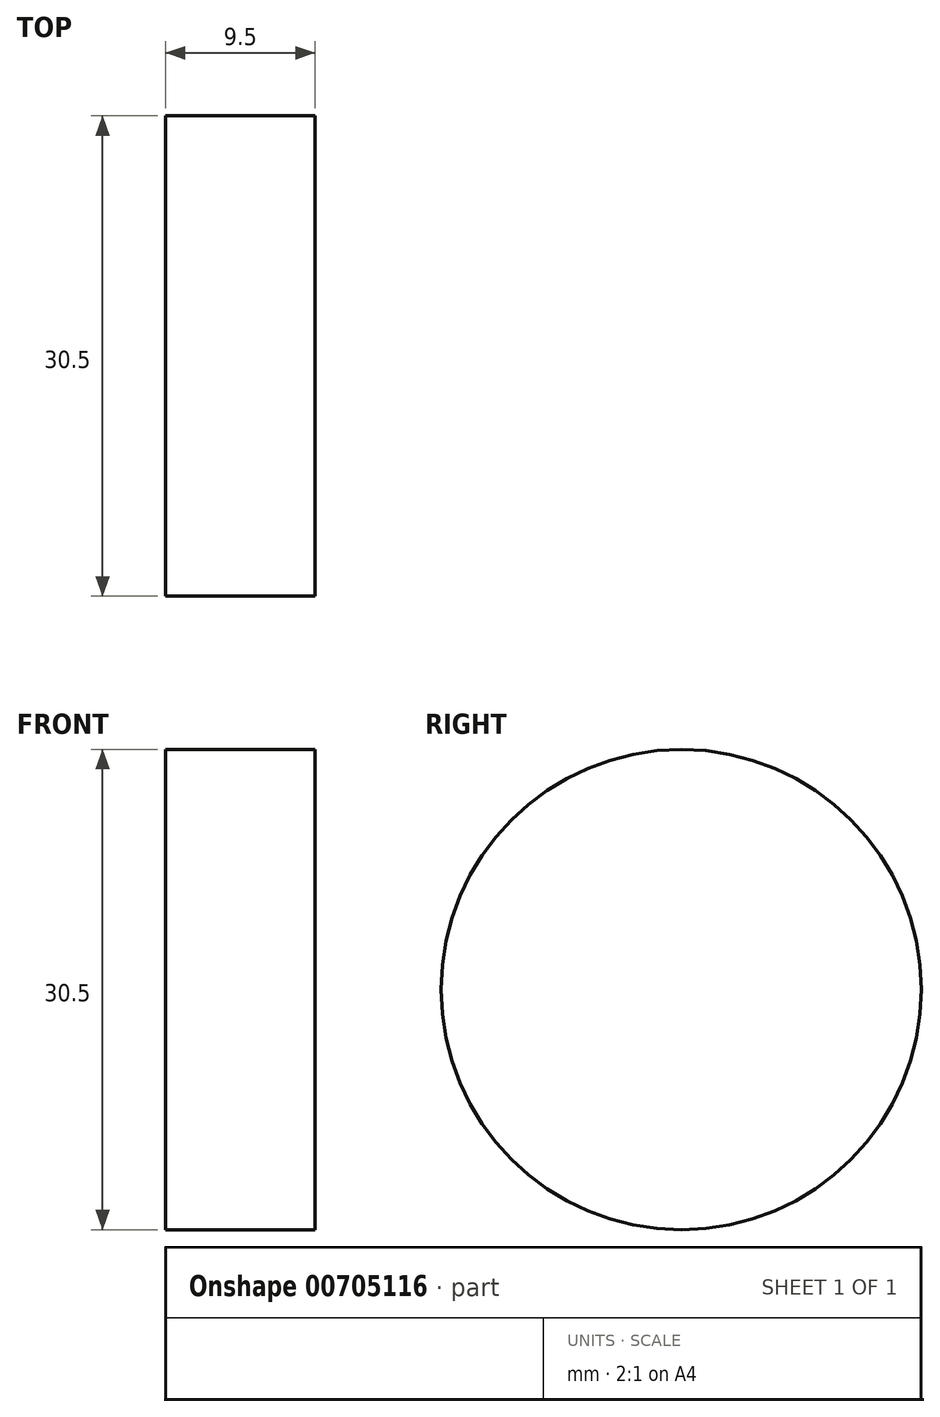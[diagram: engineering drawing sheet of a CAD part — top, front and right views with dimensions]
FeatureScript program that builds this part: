
annotation { "Feature Type Name" : "Feature", "Feature Type Description" : "" }
export const myFeature = defineFeature(function(context is Context, id is Id, definition is map)
    precondition{}
    {
        {
            var Q0;
            Q0=qCreatedBy(makeId("Right.planeOp"),FACE);
            var sketch = newSketch(context, id + "F0", { "sketchPlane" : qUnion([Q0])});
            skCircle(sketch, "E0", {"center": v(0, 0) * mm, "radius": 15.25 * mm});
            skSolve(sketch);
        }
        {
            var Q0;
            Q0=makeQuery(id+"F0.imprint","IMPRINT",FACE,{"disambiguationData":[TD([[makeQuery(id+"F0.imprint","IMPRINT",EDGE,{"derivedFrom":sQuery(id+"F0.wireOp",EDGE,"E0")}),1.0]])]});
            extrude(context, id + "F1", {"entities" : qUnion([Q0]), "endBound" : BoundingType.SYMMETRIC, "depth" : 9.5 * mm, "offsetDistance" : 25 * mm});
        }
    });
